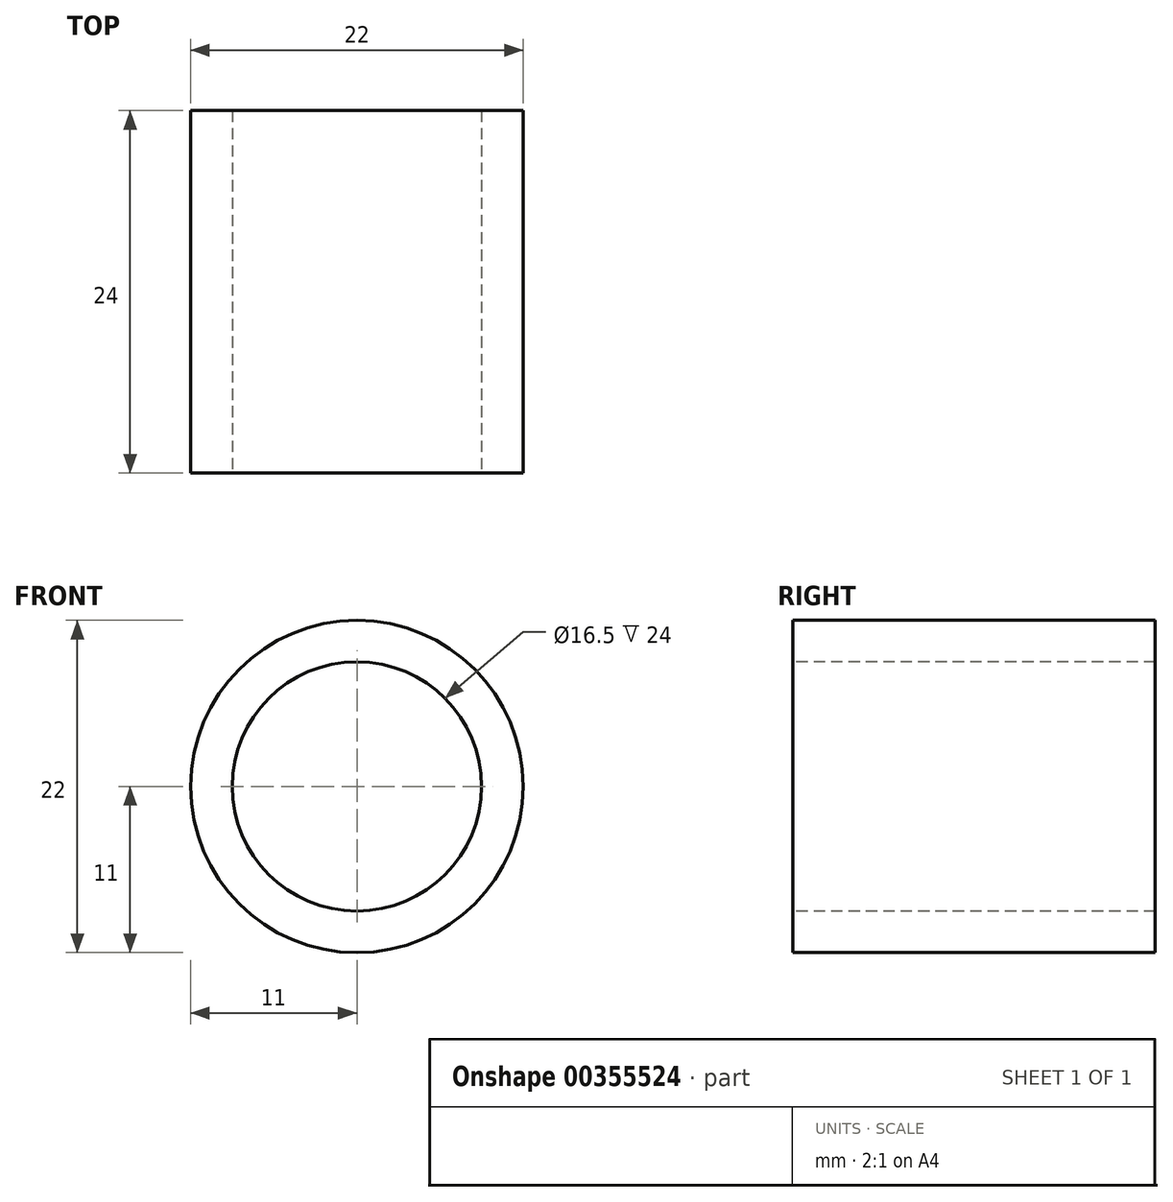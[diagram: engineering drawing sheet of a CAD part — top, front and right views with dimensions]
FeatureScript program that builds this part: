
annotation { "Feature Type Name" : "Feature", "Feature Type Description" : "" }
export const myFeature = defineFeature(function(context is Context, id is Id, definition is map)
    precondition{}
    {
        {
            var Q0;
            Q0=qCreatedBy(makeId("Front.planeOp"),FACE);
            var sketch = newSketch(context, id + "F0", { "sketchPlane" : qUnion([Q0])});
            skCircle(sketch, "E0", {"center": v(0, 0) * mm, "radius": 11 * mm});
            skCircle(sketch, "E1", {"center": v(0, 0) * mm, "radius": 8.25 * mm});
            skSolve(sketch);
        }
        {
            var Q0;
            Q0 = qSketchRegion(id + "F0", true);
            extrude(context, id + "F1", {"entities" : qUnion([Q0]), "oppositeDirection" : true, "depth" : 24 * mm});
        }
    });
